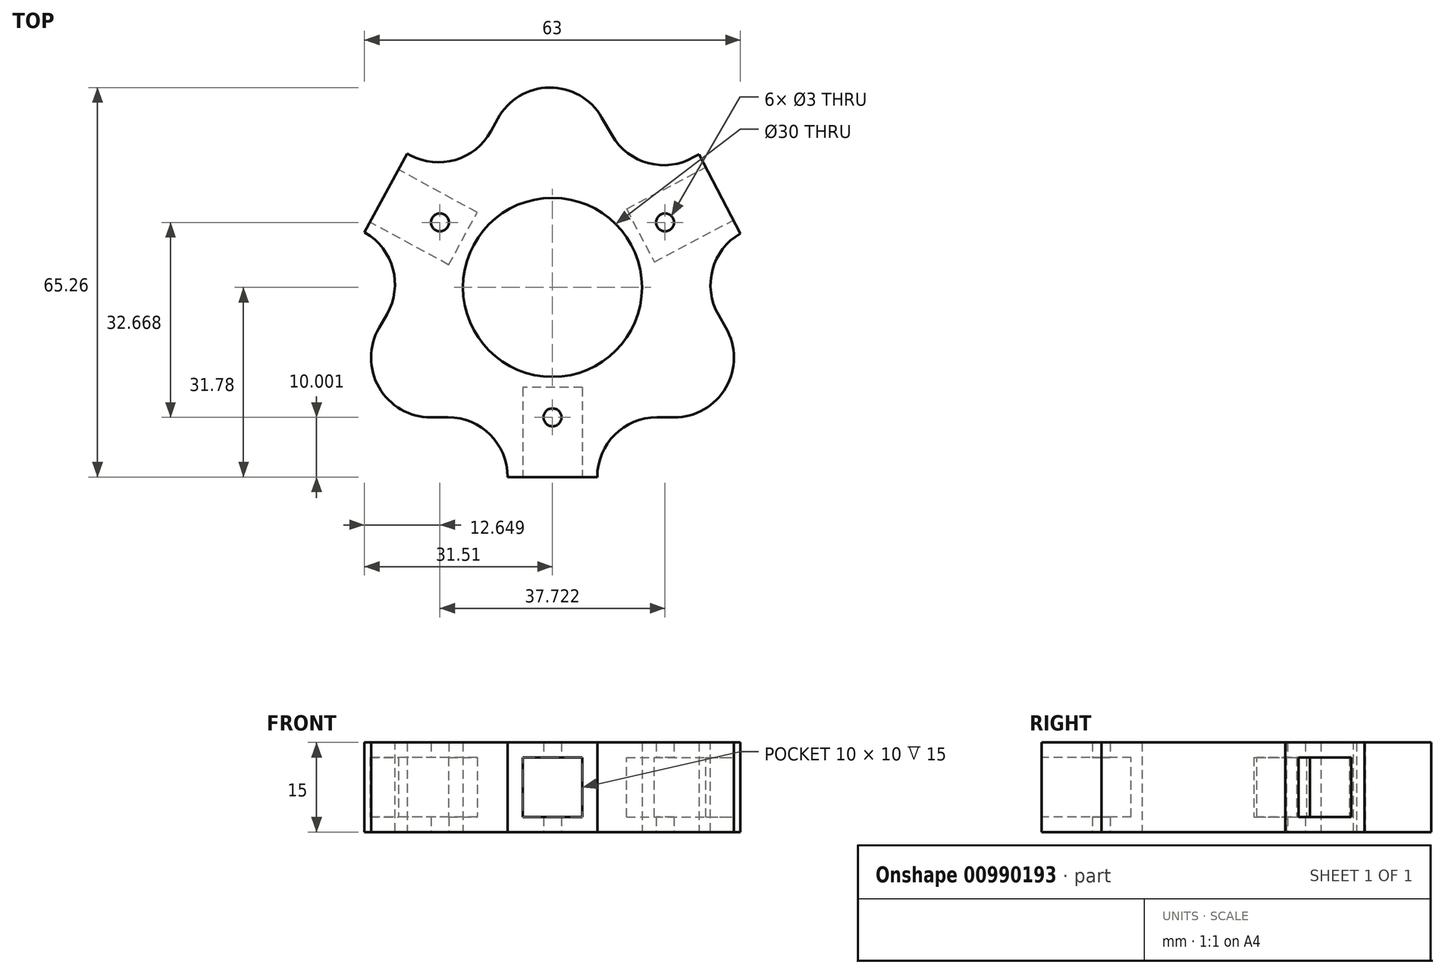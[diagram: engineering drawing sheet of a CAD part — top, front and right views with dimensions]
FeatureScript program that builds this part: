
annotation { "Feature Type Name" : "Feature", "Feature Type Description" : "" }
export const myFeature = defineFeature(function(context is Context, id is Id, definition is map)
    precondition{}
    {
        {
            var Q0;
            Q0=qCreatedBy(makeId("Top.planeOp"),FACE);
            var sketch = newSketch(context, id + "F0", { "sketchPlane" : qUnion([Q0])});
            skCircle(sketch, "E0.cCircle", {"center": v(0, 0) * mm, "radius": 21.78 * mm, "construction": true});
            skPoint(sketch, "E0.0.midPoint", {"position": v(0, -21.78) * mm});
            skLineSegment(sketch, "E1.2", {"start": v(-31.51, 9.24) * mm, "end": v(-24.34, 22.41) * mm});
            skLineSegment(sketch, "E2", {"start": v(-24.34, 22.41) * mm, "end": v(-15.1, 17.39) * mm});
            skLineSegment(sketch, "E3", {"start": v(-31.51, 9.24) * mm, "end": v(-22.74, 4.17) * mm});
            skLineSegment(sketch, "E4", {"start": v(-0.66, 43.93) * mm, "end": v(-15.1, 17.39) * mm});
            skLineSegment(sketch, "E5", {"start": v(-22.74, 4.17) * mm, "end": v(-37.72, -21.78) * mm});
            skCircle(sketch, "E6.cCircle", {"center": v(18.86, 10.89) * mm, "radius": 12.76 * mm, "construction": true});
            skLineSegment(sketch, "E6.2", {"start": v(24.52, 22.33) * mm, "end": v(31.49, 9.04) * mm});
            skLineSegment(sketch, "E7", {"start": v(24.52, 22.33) * mm, "end": v(15, 16.82) * mm});
            skLineSegment(sketch, "E8", {"start": v(31.49, 9.04) * mm, "end": v(22.82, 4.04) * mm});
            skLineSegment(sketch, "E9", {"start": v(15, 16.82) * mm, "end": v(-0.66, 43.93) * mm});
            skLineSegment(sketch, "E10", {"start": v(22.82, 4.04) * mm, "end": v(37.72, -21.78) * mm});
            skLineSegment(sketch, "E11", {"start": v(0, -31.78) * mm, "end": v(-7.5, -31.78) * mm});
            skLineSegment(sketch, "E12", {"start": v(-7.5, -31.78) * mm, "end": v(-7.5, -21.78) * mm});
            skLineSegment(sketch, "E13", {"start": v(0, -31.78) * mm, "end": v(7.5, -31.78) * mm});
            skLineSegment(sketch, "E14", {"start": v(7.5, -31.78) * mm, "end": v(7.5, -21.78) * mm});
            skLineSegment(sketch, "E15", {"start": v(-7.5, -21.78) * mm, "end": v(-37.72, -21.78) * mm});
            skLineSegment(sketch, "E16", {"start": v(7.5, -21.78) * mm, "end": v(37.72, -21.78) * mm});
            skCircle(sketch, "E17", {"center": v(0, 0) * mm, "radius": 15 * mm});
            skCircle(sketch, "E18", {"center": v(0, -21.78) * mm, "radius": 1.5 * mm});
            skCircle(sketch, "E19", {"center": v(18.86, 10.89) * mm, "radius": 1.5 * mm});
            skCircle(sketch, "E20", {"center": v(-18.86, 10.89) * mm, "radius": 1.5 * mm});
            skSolve(sketch);
        }
        {
            var Q0;
            Q0 = qSketchRegion(id + "F0", true);
            extrude(context, id + "F1", {"entities" : qUnion([Q0]), "depth" : 15 * mm, "offsetDistance" : 25 * mm});
        }
        {
            var Q0;
            Q0=makeQuery(id+"F1.opExtrude","SWEPT_FACE",FACE,{"disambiguationData":[OSD([sQuery(id+"F0.wireOp",EDGE,"E11"),sQuery(id+"F0.wireOp",EDGE,"E13")])]});
            var sketch = newSketch(context, id + "F2", { "sketchPlane" : qUnion([Q0])});
            skLineSegment(sketch, "E21.bottom", {"start": v(5, 2.5) * mm, "end": v(-5, 2.5) * mm});
            skLineSegment(sketch, "E21.top", {"start": v(5, 12.5) * mm, "end": v(-5, 12.5) * mm});
            skLineSegment(sketch, "E21.left", {"start": v(5, 2.5) * mm, "end": v(5, 12.5) * mm});
            skLineSegment(sketch, "E21.right", {"start": v(-5, 2.5) * mm, "end": v(-5, 12.5) * mm});
            skPoint(sketch, "E21.middle", {"position": v(0, 7.5) * mm});
            skSolve(sketch);
        }
        {
            var Q0;
            Q0=makeQuery(id+"F2.imprint","IMPRINT",FACE,{"disambiguationData":[TD([[makeQuery(id+"F2.imprint","IMPRINT",EDGE,{"derivedFrom":sQuery(id+"F2.wireOp",EDGE,"E21.bottom")}),-1.0]])]});
            extrude(context, id + "F3", {"entities" : qUnion([Q0]), "operationType" : NewBodyOperationType.REMOVE, "oppositeDirection" : true, "depth" : 15 * mm, "offsetDistance" : 25 * mm});
        }
        {
            var Q0;
            Q0=makeQuery(id+"F1.opExtrude","SWEPT_FACE",FACE,{"disambiguationData":[OSD([sQuery(id+"F0.wireOp",EDGE,"E1.2")])]});
            var sketch = newSketch(context, id + "F4", { "sketchPlane" : qUnion([Q0])});
            skLineSegment(sketch, "E22.bottom", {"start": v(5, 12.5) * mm, "end": v(-5, 12.5) * mm});
            skLineSegment(sketch, "E22.top", {"start": v(5, 2.5) * mm, "end": v(-5, 2.5) * mm});
            skLineSegment(sketch, "E22.left", {"start": v(5, 12.5) * mm, "end": v(5, 2.5) * mm});
            skLineSegment(sketch, "E22.right", {"start": v(-5, 12.5) * mm, "end": v(-5, 2.5) * mm});
            skPoint(sketch, "E22.middle", {"position": v(0, 7.5) * mm});
            skPoint(sketch, "E22.middle.positionSnap0", {"position": v(6.96, 7.5) * mm});
            skPoint(sketch, "E22.centerSnap0", {"position": v(6.96, 7.5) * mm});
            skSolve(sketch);
        }
        {
            var Q0;
            Q0 = qSketchRegion(id + "F4", true);
            extrude(context, id + "F5", {"entities" : qUnion([Q0]), "operationType" : NewBodyOperationType.REMOVE, "oppositeDirection" : true, "depth" : 15 * mm, "offsetDistance" : 25 * mm});
        }
        {
            var Q0;
            Q0=makeQuery(id+"F1.opExtrude","SWEPT_FACE",FACE,{"disambiguationData":[OSD([sQuery(id+"F0.wireOp",EDGE,"E6.2")])]});
            var sketch = newSketch(context, id + "F6", { "sketchPlane" : qUnion([Q0])});
            skLineSegment(sketch, "E23.bottom", {"start": v(5.89, 2.5) * mm, "end": v(-4.11, 2.5) * mm});
            skLineSegment(sketch, "E23.top", {"start": v(5.89, 12.5) * mm, "end": v(-4.11, 12.5) * mm});
            skLineSegment(sketch, "E23.left", {"start": v(5.89, 2.5) * mm, "end": v(5.89, 12.5) * mm});
            skLineSegment(sketch, "E23.right", {"start": v(-4.11, 2.5) * mm, "end": v(-4.11, 12.5) * mm});
            skPoint(sketch, "E23.middle", {"position": v(0.89, 7.5) * mm});
            skPoint(sketch, "E23.middle.positionSnap0", {"position": v(-6.61, 7.5) * mm});
            skPoint(sketch, "E23.middle.positionSnap1", {"position": v(0.89, 15) * mm});
            skPoint(sketch, "E23.centerSnap0", {"position": v(-6.61, 7.5) * mm});
            skPoint(sketch, "E23.centerSnap1", {"position": v(0.89, 15) * mm});
            skSolve(sketch);
        }
        {
            var Q0;
            Q0 = qSketchRegion(id + "F6", true);
            extrude(context, id + "F7", {"entities" : qUnion([Q0]), "operationType" : NewBodyOperationType.REMOVE, "oppositeDirection" : true, "depth" : 15 * mm, "offsetDistance" : 25 * mm});
        }
        {
            var Q0;
            Q0=makeQuery(id+"F1.opExtrude","SWEPT_EDGE",EDGE,{"disambiguationData":[OSD([sQuery(id+"F0.wireOp",EDGE,"E10"),sQuery(id+"F0.wireOp",EDGE,"E16")])]});
            var Q1;
            Q1=makeQuery(id+"F1.opExtrude","SWEPT_EDGE",EDGE,{"disambiguationData":[OSD([sQuery(id+"F0.wireOp",EDGE,"E4"),sQuery(id+"F0.wireOp",EDGE,"E9")])]});
            var Q2;
            Q2=makeQuery(id+"F1.opExtrude","SWEPT_EDGE",EDGE,{"disambiguationData":[OSD([sQuery(id+"F0.wireOp",EDGE,"E7"),sQuery(id+"F0.wireOp",EDGE,"E9")])]});
            var Q3;
            Q3=makeQuery(id+"F1.opExtrude","SWEPT_EDGE",EDGE,{"disambiguationData":[OSD([sQuery(id+"F0.wireOp",EDGE,"E8"),sQuery(id+"F0.wireOp",EDGE,"E10")])]});
            var Q4;
            Q4=makeQuery(id+"F1.opExtrude","SWEPT_EDGE",EDGE,{"disambiguationData":[OSD([sQuery(id+"F0.wireOp",EDGE,"E14"),sQuery(id+"F0.wireOp",EDGE,"E16")])]});
            var Q5;
            Q5=makeQuery(id+"F1.opExtrude","SWEPT_EDGE",EDGE,{"disambiguationData":[OSD([sQuery(id+"F0.wireOp",EDGE,"E12"),sQuery(id+"F0.wireOp",EDGE,"E15")])]});
            var Q6;
            Q6=makeQuery(id+"F1.opExtrude","SWEPT_EDGE",EDGE,{"disambiguationData":[OSD([sQuery(id+"F0.wireOp",EDGE,"E5"),sQuery(id+"F0.wireOp",EDGE,"E15")])]});
            var Q7;
            Q7=makeQuery(id+"F1.opExtrude","SWEPT_EDGE",EDGE,{"disambiguationData":[OSD([sQuery(id+"F0.wireOp",EDGE,"E3"),sQuery(id+"F0.wireOp",EDGE,"E5")])]});
            var Q8;
            Q8=makeQuery(id+"F1.opExtrude","SWEPT_EDGE",EDGE,{"disambiguationData":[OSD([sQuery(id+"F0.wireOp",EDGE,"E2"),sQuery(id+"F0.wireOp",EDGE,"E4")])]});
            fillet(context, id + "F8", {"entities" : qUnion([Q0, Q1, Q2, Q3, Q4, Q5, Q6, Q7, Q8]), "radius" : 10 * mm, "tangentPropagation" : true, "allowEdgeOverflow" : false});
        }
    });
